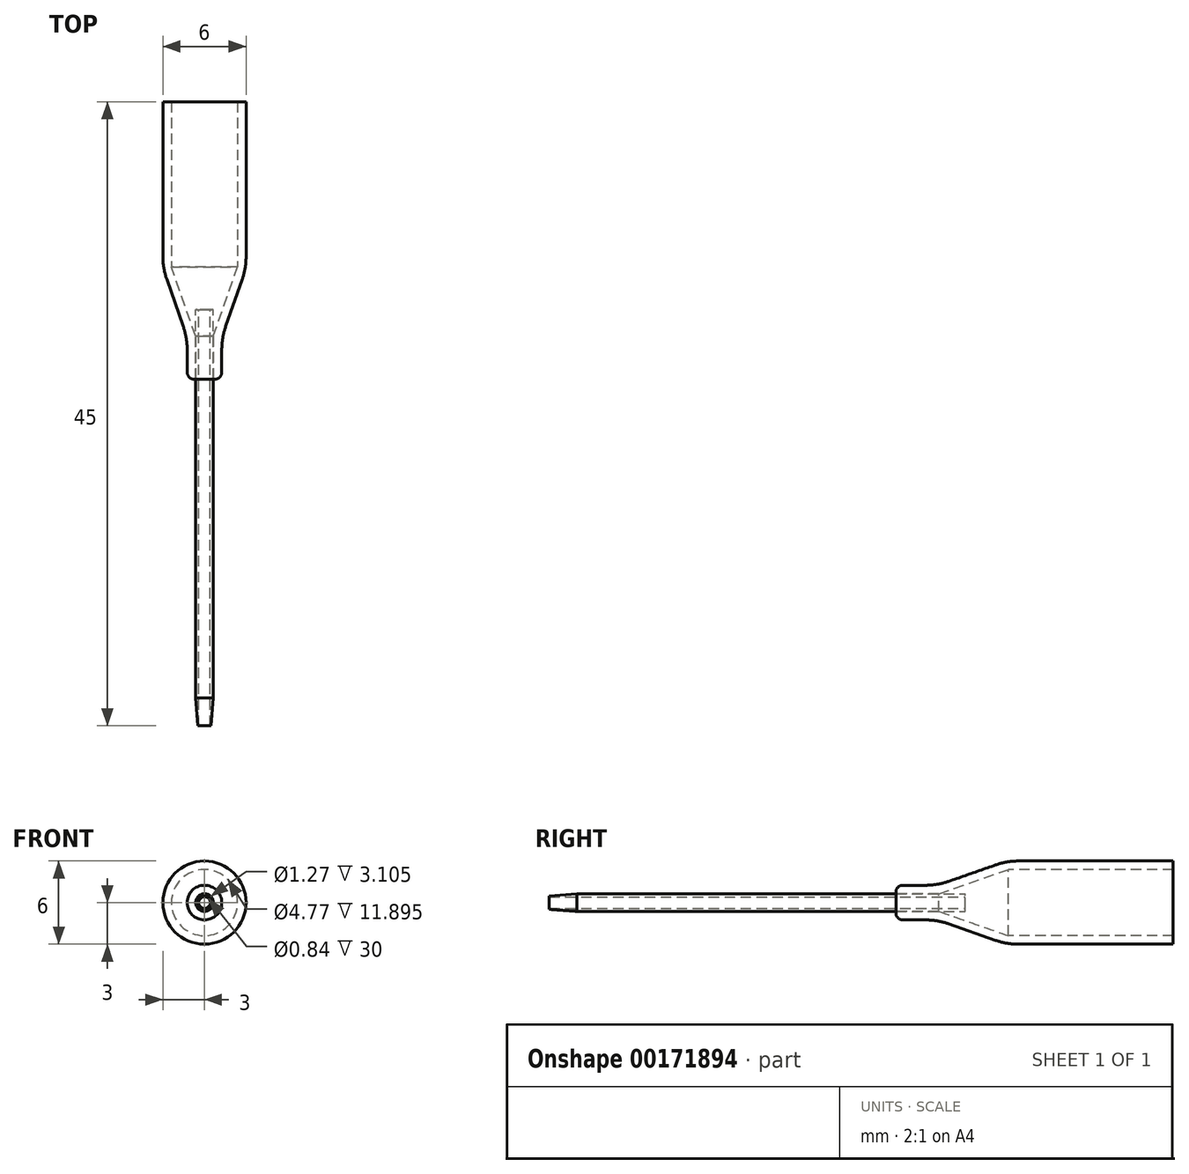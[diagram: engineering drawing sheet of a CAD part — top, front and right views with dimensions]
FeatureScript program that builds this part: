
annotation { "Feature Type Name" : "Feature", "Feature Type Description" : "" }
export const myFeature = defineFeature(function(context is Context, id is Id, definition is map)
    precondition{}
    {
        {
            var Q0;
            Q0=qCreatedBy(makeId("Front.planeOp"),FACE);
            var sketch = newSketch(context, id + "F0", { "sketchPlane" : qUnion([Q0])});
            skCircle(sketch, "E0", {"center": v(0, 0) * mm, "radius": 0.64 * mm});
            skCircle(sketch, "E1", {"center": v(0, 0) * mm, "radius": 0.42 * mm});
            skSolve(sketch);
        }
        {
            var Q0;
            Q0 = qSketchRegion(id + "F0", true);
            extrude(context, id + "F1", {"entities" : qUnion([Q0]), "depth" : 25 * mm, "hasSecondDirection" : true, "secondDirectionOppositeDirection" : true, "secondDirectionDepth" : 5 * mm});
        }
        {
            var Q0;
            Q0=qCreatedBy(makeId("Right.planeOp"),FACE);
            var sketch = newSketch(context, id + "F2", { "sketchPlane" : qUnion([Q0])});
            skLineSegment(sketch, "E2", {"start": v(0, 1.25) * mm, "end": v(3, 1.25) * mm});
            skLineSegment(sketch, "E3", {"start": v(3, 1.25) * mm, "end": v(8, 3) * mm});
            skLineSegment(sketch, "E4", {"start": v(8, 3) * mm, "end": v(20, 3) * mm});
            skLineSegment(sketch, "E5", {"start": v(20, 3) * mm, "end": v(20, 2.39) * mm});
            skLineSegment(sketch, "E6", {"start": v(20, 2.39) * mm, "end": v(8.1, 2.38) * mm});
            skLineSegment(sketch, "E7", {"start": v(8.1, 2.38) * mm, "end": v(3.1, 0.64) * mm});
            skLineSegment(sketch, "E8", {"start": v(0, 1.25) * mm, "end": v(0, 0.64) * mm});
            skLineSegment(sketch, "E9", {"start": v(0, 0.64) * mm, "end": v(3.1, 0.64) * mm});
            skLineSegment(sketch, "E10", {"start": v(0, 0) * mm, "end": v(15.98, 0) * mm, "construction": true});
            skLineSegment(sketch, "E11", {"start": v(7.9, 2.97) * mm, "end": v(8.1, 2.38) * mm, "construction": true});
            skSolve(sketch);
        }
        {
            var Q0;
            Q0=makeQuery(id+"F2.imprint","IMPRINT",FACE,{"disambiguationData":[TD([[makeQuery(id+"F2.imprint","IMPRINT",EDGE,{"derivedFrom":sQuery(id+"F2.wireOp",EDGE,"E2")}),-1.0]])]});
            var Q1;
            Q1=sQuery(id+"F2.wireOp",EDGE,"E10");
            revolve(context, id + "F3", {"entities" : qUnion([Q0]), "axis" : qUnion([Q1]), "revolveType" : RevolveType.FULL});
        }
        {
            var Q0;
            Q0=makeQuery(id+"F3.opRevolve","SWEPT_EDGE",EDGE,{"disambiguationData":[OSD([sQuery(id+"F2.wireOp",EDGE,"E2"),sQuery(id+"F2.wireOp",EDGE,"E8")])]});
            fillet(context, id + "F4", {"entities" : qUnion([Q0]), "radius" : .5 * mm, "tangentPropagation" : true, "allowEdgeOverflow" : false});
        }
        {
            var Q0;
            Q0=makeQuery(id+"F3.opRevolve","SWEPT_EDGE",EDGE,{"disambiguationData":[OSD([sQuery(id+"F2.wireOp",EDGE,"E3"),sQuery(id+"F2.wireOp",EDGE,"E4")])]});
            var Q1;
            Q1=makeQuery(id+"F3.opRevolve","SWEPT_EDGE",EDGE,{"disambiguationData":[OSD([sQuery(id+"F2.wireOp",EDGE,"E2"),sQuery(id+"F2.wireOp",EDGE,"E3")])]});
            fillet(context, id + "F5", {"entities" : qUnion([Q0, Q1]), "radius" : 5 * mm, "tangentPropagation" : true, "allowEdgeOverflow" : false});
        }
        {
            var Q0;
            Q0=makeQuery(id+"F1.opExtrude","CAP_EDGE",EDGE,{"disambiguationData":[OSD([sQuery(id+"F0.wireOp",EDGE,"E0")])],"isStart":false});
            chamfer(context, id + "F6", {"entities" : qUnion([Q0]), "chamferType" : ChamferType.TWO_OFFSETS, "width1" : .15 * mm, "oppositeDirection" : false, "width2" : 2 * mm, "tangentPropagation" : true});
        }
    });
